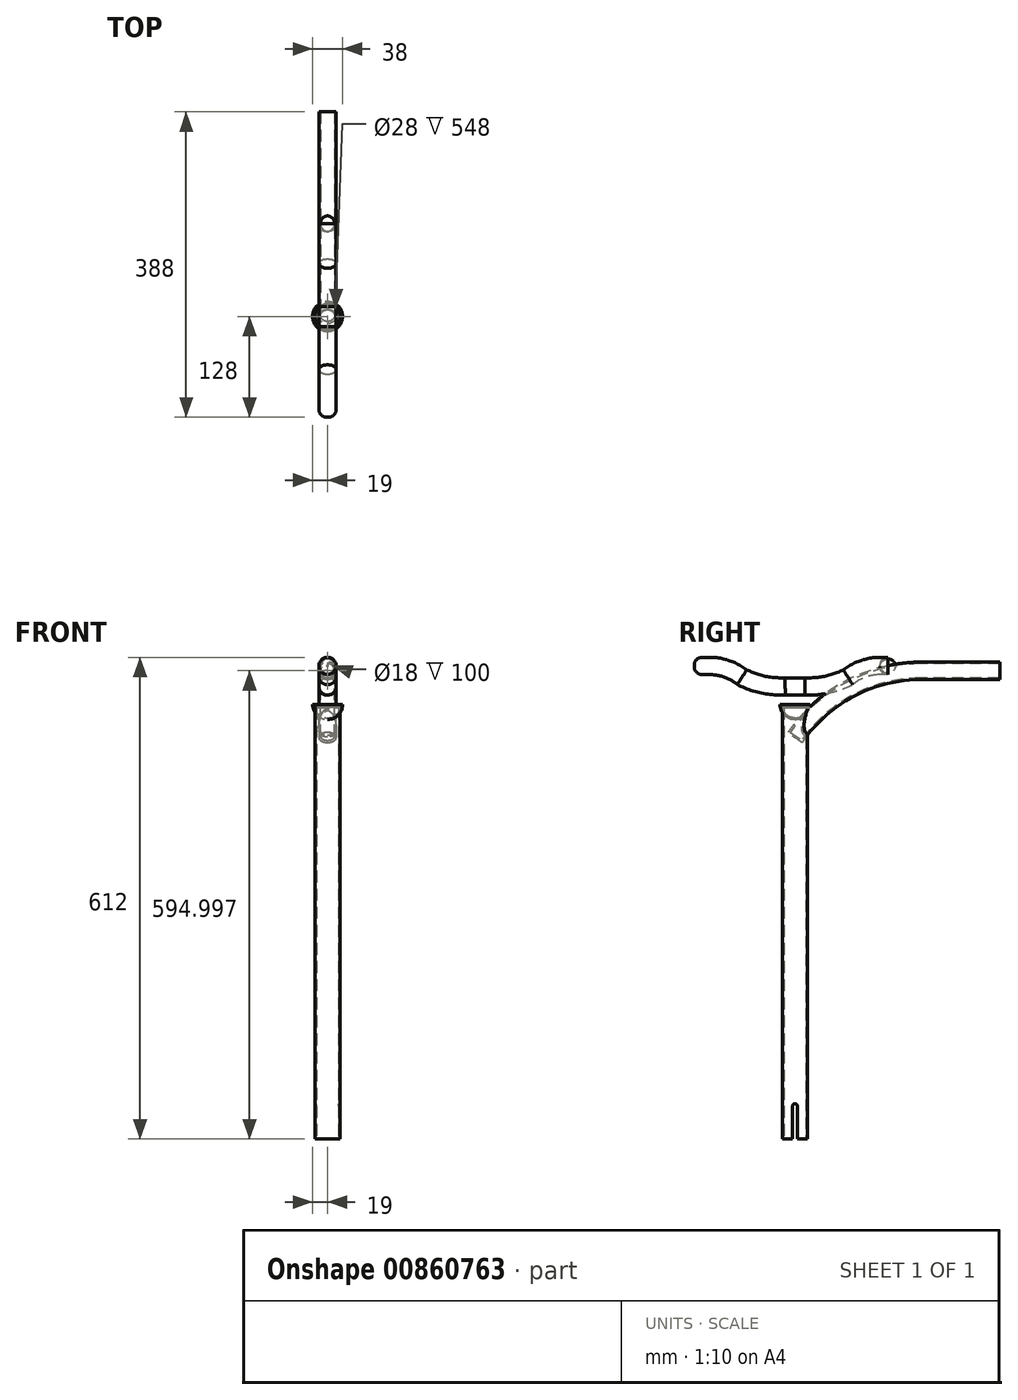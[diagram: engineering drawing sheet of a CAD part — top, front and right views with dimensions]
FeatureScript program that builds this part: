
annotation { "Feature Type Name" : "Feature", "Feature Type Description" : "" }
export const myFeature = defineFeature(function(context is Context, id is Id, definition is map)
    precondition{}
    {
        {
            var Q0;
            Q0=qCreatedBy(makeId("Top.planeOp"),FACE);
            var sketch = newSketch(context, id + "F0", { "sketchPlane" : qUnion([Q0])});
            skCircle(sketch, "E0", {"center": v(0, 0) * mm, "radius": 16 * mm});
            skSolve(sketch);
        }
        {
            var Q0;
            Q0=makeQuery(id+"F0.imprint","IMPRINT",FACE,{"disambiguationData":[TD([[makeQuery(id+"F0.imprint","IMPRINT",EDGE,{"derivedFrom":sQuery(id+"F0.wireOp",EDGE,"E0")}),1.0]])]});
            extrude(context, id + "F1", {"entities" : qUnion([Q0]), "depth" : 550 * mm, "offsetDistance" : 25 * mm});
        }
        {
            var Q0;
            Q0=makeQuery(id+"F1.opExtrude","CAP_FACE",FACE,{"disambiguationData":[OSD([sQuery(id+"F0.wireOp",EDGE,"E0")])],"isStart":true});
            shell(context, id + "F2", {"entities" : qUnion([Q0]), "thickness" : 2 * mm});
        }
        {
            var Q0;
            Q0=qCreatedBy(makeId("Right.planeOp"),FACE);
            var sketch = newSketch(context, id + "F3", { "sketchPlane" : qUnion([Q0])});
            skLineSegment(sketch, "E1.bottom", {"start": v(-3, 0) * mm, "end": v(3, 0) * mm});
            skLineSegment(sketch, "E1.top", {"start": v(0, 45) * mm, "end": v(0, 45) * mm});
            skLineSegment(sketch, "E1.left", {"start": v(-3, 0) * mm, "end": v(-3, 42) * mm});
            skLineSegment(sketch, "E1.right", {"start": v(3, 0) * mm, "end": v(3, 42) * mm});
            skPoint(sketch, "E2.visualSharp", {"position": v(-3, 45) * mm});
            skArc(sketch, "E2.filletArc", {"start": v(0, 45) * mm, "mid": v(-2.12, 44.12) * mm, "end": v(-3, 42) * mm});
            skPoint(sketch, "E3.visualSharp", {"position": v(3, 45) * mm});
            skArc(sketch, "E3.filletArc", {"start": v(3, 42) * mm, "mid": v(2.12, 44.12) * mm, "end": v(0, 45) * mm});
            skSolve(sketch);
        }
        {
            var Q0;
            Q0=qSketchRegion(id+"F3",true);
            extrude(context, id + "F4", {"entities" : qUnion([Q0]), "operationType" : NewBodyOperationType.REMOVE, "endBound" : BoundingType.SYMMETRIC, "depth" : 35 * mm, "offsetDistance" : 25 * mm});
        }
        {
            var Q0;
            Q0=qCreatedBy(makeId("Right.planeOp"),FACE);
            var sketch = newSketch(context, id + "F5", { "sketchPlane" : qUnion([Q0])});
            skArc(sketch, "E4", {"start": v(160, 595) * mm, "mid": v(69.53, 572.2) * mm, "end": v(0, 510) * mm});
            skLineSegment(sketch, "E5", {"start": v(160, 595) * mm, "end": v(260, 595) * mm});
            skLineSegment(sketch, "E6", {"start": v(0, 550) * mm, "end": v(0, 510) * mm, "construction": true});
            skSolve(sketch);
        }
        {
            var Q0;
            Q0=sQuery(id+"F5.wireOp",VERTEX,"E5.end");
            var Q1;
            Q1=qCreatedBy(makeId("Front.planeOp"),FACE);
            cPlane(context, id + "F6", {"entities" : qUnion([Q0, Q1]), "cplaneType" : CPlaneType.PLANE_POINT, "offset" : 25 * mm, "width" : 150 * mm, "height" : 150 * mm});
        }
        {
            var Q0;
            Q0=qCreatedBy(id+"F6.planeOp",FACE);
            var sketch = newSketch(context, id + "F7", { "sketchPlane" : qUnion([Q0])});
            skCircle(sketch, "E7", {"center": v(0, 595) * mm, "radius": 11 * mm});
            skSolve(sketch);
        }
        {
            var Q0;
            Q0=qSketchRegion(id+"F7",true);
            var Q1;
            Q1=qConstructionFilter(qBodyType(qCreatedBy(id+"F5",EDGE),BodyType.WIRE),ConstructionObject.NO);
            sweep(context, id + "F8", {"operationType" : NewBodyOperationType.ADD, "profiles" : qUnion([Q0]), "path" : qUnion([Q1])});
        }
        {
            var Q0;
            Q0=makeQuery(id+"F8.opSweep","CAP_FACE",FACE,{"disambiguationData":[OSD([sQuery(id+"F5.wireOp",VERTEX,"E5.end"),sQuery(id+"F7.wireOp",EDGE,"E7")])],"isStart":true});
            shell(context, id + "F9", {"entities" : qUnion([Q0]), "thickness" : 2 * mm});
        }
        {
            var Q0;
            Q0=qCreatedBy(makeId("Right.planeOp"),FACE);
            var sketch = newSketch(context, id + "F10", { "sketchPlane" : qUnion([Q0])});
            skLineSegment(sketch, "E8", {"start": v(0, 575) * mm, "end": v(0, 0) * mm, "construction": true});
            skLineSegment(sketch, "E9", {"start": v(-128, 601) * mm, "end": v(-108, 601) * mm});
            skArc(sketch, "E10", {"start": v(-67.24, 586.71) * mm, "mid": v(-86.4, 597.33) * mm, "end": v(-108, 601) * mm});
            skArc(sketch, "E11", {"start": v(-67.24, 586.71) * mm, "mid": v(-40.62, 577.38) * mm, "end": v(-12.5, 575) * mm});
            skLineSegment(sketch, "E12", {"start": v(-12.5, 575) * mm, "end": v(0, 575) * mm});
            skLineSegment(sketch, "E13.MirrorCS", {"start": v(12.5, 575) * mm, "end": v(0, 575) * mm});
            skArc(sketch, "E14.MirrorCS", {"start": v(67.24, 586.71) * mm, "mid": v(40.62, 577.38) * mm, "end": v(12.5, 575) * mm});
            skArc(sketch, "E15.MirrorCS", {"start": v(67.24, 586.71) * mm, "mid": v(86.4, 597.33) * mm, "end": v(108, 601) * mm});
            skLineSegment(sketch, "E16.MirrorCS", {"start": v(128, 601) * mm, "end": v(108, 601) * mm});
            skSolve(sketch);
        }
        {
            var Q0;
            Q0=sQuery(id+"F10.wireOp",VERTEX,"E16.MirrorCS.start");
            var Q1;
            Q1=qCreatedBy(id+"F6.planeOp",FACE);
            cPlane(context, id + "F11", {"entities" : qUnion([Q0, Q1]), "cplaneType" : CPlaneType.PLANE_POINT, "offset" : 25 * mm, "width" : 150 * mm, "height" : 150 * mm});
        }
        {
            var Q0;
            Q0=qCreatedBy(id+"F11.planeOp",FACE);
            var sketch = newSketch(context, id + "F12", { "sketchPlane" : qUnion([Q0])});
            skCircle(sketch, "E17", {"center": v(0, 601) * mm, "radius": 11 * mm});
            skSolve(sketch);
        }
        {
            var Q0;
            Q0=qSketchRegion(id+"F12",true);
            var Q1;
            Q1=qConstructionFilter(qBodyType(qCreatedBy(id+"F10",EDGE),BodyType.WIRE),ConstructionObject.NO);
            sweep(context, id + "F13", {"profiles" : qUnion([Q0]), "path" : qUnion([Q1])});
        }
        {
            var Q0;
            Q0=makeQuery(id+"F13.opSweep","CAP_EDGE",EDGE,{"disambiguationData":[OSD([sQuery(id+"F10.wireOp",VERTEX,"E9.start"),sQuery(id+"F12.wireOp",EDGE,"E17")])],"isStart":false});
            var Q1;
            Q1=makeQuery(id+"F13.opSweep","CAP_EDGE",EDGE,{"disambiguationData":[OSD([sQuery(id+"F10.wireOp",VERTEX,"E16.MirrorCS.start"),sQuery(id+"F12.wireOp",EDGE,"E17")])],"isStart":true});
            fillet(context, id + "F14", {"entities" : qUnion([Q0, Q1]), "radius" : 10 * mm, "tangentPropagation" : true, "allowEdgeOverflow" : false});
        }
        {
            var Q0;
            Q0=qCreatedBy(makeId("Right.planeOp"),FACE);
            var sketch = newSketch(context, id + "F15", { "sketchPlane" : qUnion([Q0])});
            skArc(sketch, "E18", {"start": v(-19, 552) * mm, "mid": v(-13.44, 538.56) * mm, "end": v(0, 533) * mm});
            skLineSegment(sketch, "E19", {"start": v(0, 552) * mm, "end": v(0, 533) * mm});
            skLineSegment(sketch, "E20", {"start": v(-19, 552) * mm, "end": v(0, 552) * mm});
            skPoint(sketch, "E21.orphan", {"position": v(0, 571) * mm});
            skSolve(sketch);
        }
        {
            var Q0;
            Q0=qSketchRegion(id+"F15",true);
            var Q1;
            Q1=sQuery(id+"F15.wireOp",EDGE,"E19");
            revolve(context, id + "F16", {"surfaceOperationType" : NewSurfaceOperationType.NEW, "entities" : qUnion([Q0]), "axis" : qUnion([Q1]), "revolveType" : RevolveType.FULL});
        }
        {
            var Q0;
            Q0=makeQuery(id+"F16.opRevolve","SWEPT_FACE",FACE,{"disambiguationData":[OSD([sQuery(id+"F15.wireOp",EDGE,"E20")])]});
            shell(context, id + "F17", {"entities" : qUnion([Q0]), "thickness" : 2 * mm});
        }
    });
